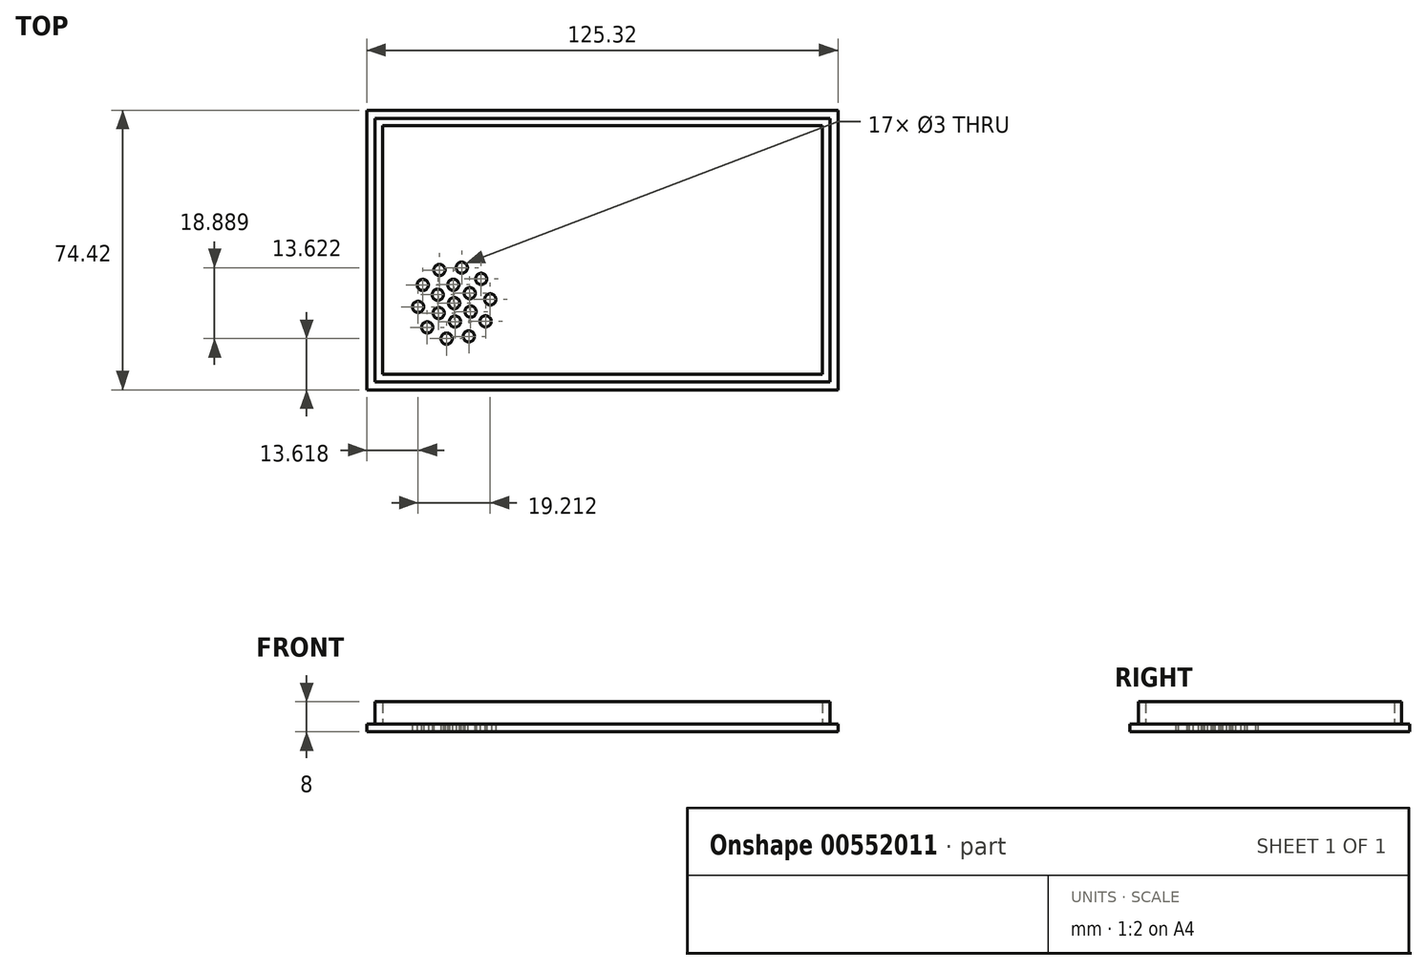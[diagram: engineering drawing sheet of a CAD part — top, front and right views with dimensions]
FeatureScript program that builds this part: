
annotation { "Feature Type Name" : "Feature", "Feature Type Description" : "" }
export const myFeature = defineFeature(function(context is Context, id is Id, definition is map)
    precondition{}
    {
        {
            var Q0;
            Q0=qCreatedBy(makeId("Top.planeOp"),FACE);
            var sketch = newSketch(context, id + "F0", { "sketchPlane" : qUnion([Q0])});
            skLineSegment(sketch, "E0.bottom", {"start": v(62.66, 37.2) * mm, "end": v(-62.66, 37.2) * mm});
            skLineSegment(sketch, "E0.top", {"start": v(62.66, -37.2) * mm, "end": v(-62.66, -37.2) * mm});
            skLineSegment(sketch, "E0.left", {"start": v(62.66, 37.2) * mm, "end": v(62.66, -37.2) * mm});
            skLineSegment(sketch, "E0.right", {"start": v(-62.66, 37.2) * mm, "end": v(-62.66, -37.2) * mm});
            skPoint(sketch, "E0.middle", {"position": v(0, 0) * mm});
            skSolve(sketch);
        }
        {
            var Q0;
            Q0=makeQuery(id+"F0.imprint","IMPRINT",FACE,{"disambiguationData":[TD([[makeQuery(id+"F0.imprint","IMPRINT",EDGE,{"derivedFrom":sQuery(id+"F0.wireOp",EDGE,"E0.bottom")}),1.0]])]});
            extrude(context, id + "F1", {"entities" : qUnion([Q0]), "depth" : 2 * mm, "offsetDistance" : 25 * mm});
        }
        {
            var Q0;
            Q0=makeQuery(id+"F1.opExtrude","CAP_FACE",FACE,{"disambiguationData":[OSD([sQuery(id+"F0.wireOp",EDGE,"E0.bottom"),sQuery(id+"F0.wireOp",EDGE,"E0.top"),sQuery(id+"F0.wireOp",EDGE,"E0.left"),sQuery(id+"F0.wireOp",EDGE,"E0.right")])],"isStart":false});
            var sketch = newSketch(context, id + "F2", { "sketchPlane" : qUnion([Q0])});
            skLineSegment(sketch, "E1.0", {"start": v(60.5, 35.04) * mm, "end": v(-60.5, 35.04) * mm});
            skLineSegment(sketch, "E1.1", {"start": v(60.5, 35.04) * mm, "end": v(60.5, -35.04) * mm});
            skLineSegment(sketch, "E1.2", {"start": v(60.5, -35.04) * mm, "end": v(-60.5, -35.04) * mm});
            skLineSegment(sketch, "E1.3", {"start": v(-60.5, 35.04) * mm, "end": v(-60.5, -35.04) * mm});
            skLineSegment(sketch, "E2.0", {"start": v(58.5, 33.04) * mm, "end": v(58.5, -33.04) * mm});
            skLineSegment(sketch, "E2.1", {"start": v(58.5, 33.04) * mm, "end": v(-58.5, 33.04) * mm});
            skLineSegment(sketch, "E2.2", {"start": v(-58.5, 33.04) * mm, "end": v(-58.5, -33.04) * mm});
            skLineSegment(sketch, "E2.3", {"start": v(58.5, -33.04) * mm, "end": v(-58.5, -33.04) * mm});
            skLineSegment(sketch, "E3", {"start": v(0, -35.04) * mm, "end": v(0, 35.06) * mm, "construction": true});
            skPoint(sketch, "E3.endSnap0", {"position": v(0, -35.04) * mm});
            skSolve(sketch);
        }
        {
            var Q0;
            Q0=makeQuery(id+"F2.imprint","IMPRINT",FACE,{"disambiguationData":[TD([[makeQuery(id+"F2.imprint","IMPRINT",EDGE,{"derivedFrom":sQuery(id+"F2.wireOp",EDGE,"E1.0")}),1.0]])]});
            extrude(context, id + "F3", {"entities" : qUnion([Q0]), "operationType" : NewBodyOperationType.ADD, "depth" : 6 * mm, "offsetDistance" : 25 * mm});
        }
        {
            var Q0;
            Q0=makeQuery(id+"F1.opExtrude","CAP_FACE",FACE,{"disambiguationData":[OSD([sQuery(id+"F0.wireOp",EDGE,"E0.bottom"),sQuery(id+"F0.wireOp",EDGE,"E0.top"),sQuery(id+"F0.wireOp",EDGE,"E0.left"),sQuery(id+"F0.wireOp",EDGE,"E0.right")])],"isStart":true});
            var sketch = newSketch(context, id + "F4", { "sketchPlane" : qUnion([Q0])});
            skCircle(sketch, "E4", {"center": v(-46.62, 20.6) * mm, "radius": 1.5 * mm});
            skCircle(sketch, "E5.1.0", {"center": v(-49.04, 15.14) * mm, "radius": 1.5 * mm});
            skCircle(sketch, "E5.2.0", {"center": v(-47.8, 9.3) * mm, "radius": 1.5 * mm});
            skCircle(sketch, "E5.3.0", {"center": v(-43.35, 5.32) * mm, "radius": 1.5 * mm});
            skCircle(sketch, "E5.4.0", {"center": v(-37.42, 4.7) * mm, "radius": 1.5 * mm});
            skCircle(sketch, "E5.5.0", {"center": v(-32.25, 7.7) * mm, "radius": 1.5 * mm});
            skCircle(sketch, "E5.6.0", {"center": v(-29.83, 13.15) * mm, "radius": 1.5 * mm});
            skCircle(sketch, "E5.7.0", {"center": v(-31.08, 18.98) * mm, "radius": 1.5 * mm});
            skCircle(sketch, "E5.8.0", {"center": v(-35.52, 22.97) * mm, "radius": 1.5 * mm});
            skCircle(sketch, "E5.9.0", {"center": v(-41.46, 23.59) * mm, "radius": 1.5 * mm});
            skPoint(sketch, "E5.center", {"position": v(-39.44, 14.14) * mm});
            skCircle(sketch, "E6", {"center": v(-39.44, 14.14) * mm, "radius": 1.5 * mm});
            skCircle(sketch, "E7", {"center": v(-39.2, 19.04) * mm, "radius": 1.5 * mm});
            skCircle(sketch, "E8.1.0", {"center": v(-43.57, 16.8) * mm, "radius": 1.5 * mm});
            skCircle(sketch, "E8.2.0", {"center": v(-43.8, 11.9) * mm, "radius": 1.5 * mm});
            skCircle(sketch, "E8.3.0", {"center": v(-39.66, 9.24) * mm, "radius": 1.5 * mm});
            skCircle(sketch, "E8.4.0", {"center": v(-35.3, 11.5) * mm, "radius": 1.5 * mm});
            skCircle(sketch, "E8.5.0", {"center": v(-35.08, 16.4) * mm, "radius": 1.5 * mm});
            skSolve(sketch);
        }
        {
            var Q0;
            Q0=makeQuery(id+"F4.imprint","IMPRINT",FACE,{"disambiguationData":[TD([[makeQuery(id+"F4.imprint","IMPRINT",EDGE,{"derivedFrom":sQuery(id+"F4.wireOp",EDGE,"E6")}),1.0]])]});
            var Q1;
            Q1=makeQuery(id+"F4.imprint","IMPRINT",FACE,{"disambiguationData":[TD([[makeQuery(id+"F4.imprint","IMPRINT",EDGE,{"derivedFrom":sQuery(id+"F4.wireOp",EDGE,"E8.5.0")}),1.0]])]});
            var Q2;
            Q2=makeQuery(id+"F4.imprint","IMPRINT",FACE,{"disambiguationData":[TD([[makeQuery(id+"F4.imprint","IMPRINT",EDGE,{"derivedFrom":sQuery(id+"F4.wireOp",EDGE,"E5.7.0")}),1.0]])]});
            var Q3;
            Q3=makeQuery(id+"F4.imprint","IMPRINT",FACE,{"disambiguationData":[TD([[makeQuery(id+"F4.imprint","IMPRINT",EDGE,{"derivedFrom":sQuery(id+"F4.wireOp",EDGE,"E5.6.0")}),1.0]])]});
            var Q4;
            Q4=makeQuery(id+"F4.imprint","IMPRINT",FACE,{"disambiguationData":[TD([[makeQuery(id+"F4.imprint","IMPRINT",EDGE,{"derivedFrom":sQuery(id+"F4.wireOp",EDGE,"E5.5.0")}),1.0]])]});
            var Q5;
            Q5=makeQuery(id+"F4.imprint","IMPRINT",FACE,{"disambiguationData":[TD([[makeQuery(id+"F4.imprint","IMPRINT",EDGE,{"derivedFrom":sQuery(id+"F4.wireOp",EDGE,"E8.4.0")}),1.0]])]});
            var Q6;
            Q6=makeQuery(id+"F4.imprint","IMPRINT",FACE,{"disambiguationData":[TD([[makeQuery(id+"F4.imprint","IMPRINT",EDGE,{"derivedFrom":sQuery(id+"F4.wireOp",EDGE,"E5.4.0")}),1.0]])]});
            var Q7;
            Q7=makeQuery(id+"F4.imprint","IMPRINT",FACE,{"disambiguationData":[TD([[makeQuery(id+"F4.imprint","IMPRINT",EDGE,{"derivedFrom":sQuery(id+"F4.wireOp",EDGE,"E5.3.0")}),1.0]])]});
            var Q8;
            Q8=makeQuery(id+"F4.imprint","IMPRINT",FACE,{"disambiguationData":[TD([[makeQuery(id+"F4.imprint","IMPRINT",EDGE,{"derivedFrom":sQuery(id+"F4.wireOp",EDGE,"E8.3.0")}),1.0]])]});
            var Q9;
            Q9=makeQuery(id+"F4.imprint","IMPRINT",FACE,{"disambiguationData":[TD([[makeQuery(id+"F4.imprint","IMPRINT",EDGE,{"derivedFrom":sQuery(id+"F4.wireOp",EDGE,"E7")}),1.0]])]});
            var Q10;
            Q10=makeQuery(id+"F4.imprint","IMPRINT",FACE,{"disambiguationData":[TD([[makeQuery(id+"F4.imprint","IMPRINT",EDGE,{"derivedFrom":sQuery(id+"F4.wireOp",EDGE,"E5.8.0")}),1.0]])]});
            var Q11;
            Q11=makeQuery(id+"F4.imprint","IMPRINT",FACE,{"disambiguationData":[TD([[makeQuery(id+"F4.imprint","IMPRINT",EDGE,{"derivedFrom":sQuery(id+"F4.wireOp",EDGE,"E5.9.0")}),1.0]])]});
            var Q12;
            Q12=makeQuery(id+"F4.imprint","IMPRINT",FACE,{"disambiguationData":[TD([[makeQuery(id+"F4.imprint","IMPRINT",EDGE,{"derivedFrom":sQuery(id+"F4.wireOp",EDGE,"E4")}),1.0]])]});
            var Q13;
            Q13=makeQuery(id+"F4.imprint","IMPRINT",FACE,{"disambiguationData":[TD([[makeQuery(id+"F4.imprint","IMPRINT",EDGE,{"derivedFrom":sQuery(id+"F4.wireOp",EDGE,"E8.1.0")}),1.0]])]});
            var Q14;
            Q14=makeQuery(id+"F4.imprint","IMPRINT",FACE,{"disambiguationData":[TD([[makeQuery(id+"F4.imprint","IMPRINT",EDGE,{"derivedFrom":sQuery(id+"F4.wireOp",EDGE,"E8.2.0")}),1.0]])]});
            var Q15;
            Q15=makeQuery(id+"F4.imprint","IMPRINT",FACE,{"disambiguationData":[TD([[makeQuery(id+"F4.imprint","IMPRINT",EDGE,{"derivedFrom":sQuery(id+"F4.wireOp",EDGE,"E5.2.0")}),1.0]])]});
            var Q16;
            Q16=makeQuery(id+"F4.imprint","IMPRINT",FACE,{"disambiguationData":[TD([[makeQuery(id+"F4.imprint","IMPRINT",EDGE,{"derivedFrom":sQuery(id+"F4.wireOp",EDGE,"E5.1.0")}),1.0]])]});
            extrude(context, id + "F5", {"entities" : qUnion([Q0, Q1, Q2, Q3, Q4, Q5, Q6, Q7, Q8, Q9, Q10, Q11, Q12, Q13, Q14, Q15, Q16]), "operationType" : NewBodyOperationType.REMOVE, "endBound" : BoundingType.THROUGH_ALL, "oppositeDirection" : true, "depth" : 25 * mm, "offsetDistance" : 25 * mm});
        }
    });
